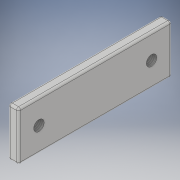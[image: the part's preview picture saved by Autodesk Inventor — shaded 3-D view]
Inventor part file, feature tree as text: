
AUTODESK INVENTOR PART (.ipt)
format: ipt  version: 2019 (Build 230136000, 136)  size: 121,856 bytes
history: native  units: in
note: dims shown in document units (in); Inventor stores cm internally (conversion verified against a paired STEP export)
features: extrude x2, sketch x2, thread x1, mirror x1, fillet x1
ambient origin geometry x8: Origin, YZ Plane, XZ Plane, XY Plane, X Axis, Y Axis, Z Axis, Center Point
bodies: Solid1 (feature_tree)
feature tree (7):
  extrude  "Extrusion1"  Depth=0.5512in
  extrude  "Extrusion2"  Depth=0.0236in
  thread  "Thread1"  [1 undecoded]
  mirror  "Mirror1"
  fillet  "Fillet1"  Radius=0.1181in
  sketch  "Sketch1"  dims[d0=1.7323in d1=0.5512in]
  sketch  "Sketch2"  dims[d2=0.1181in d3=0.0in d4=0.636in d5=0.1181in d6=0.1181in d7=0.0in d8=0.3937in d9=0.0in d10=0.0236in]
note: 1 required parameter value undecoded (feature->parameter linkage not recoverable at this tier; creation-order binding heuristic only, values carry confidence <= 0.55)
